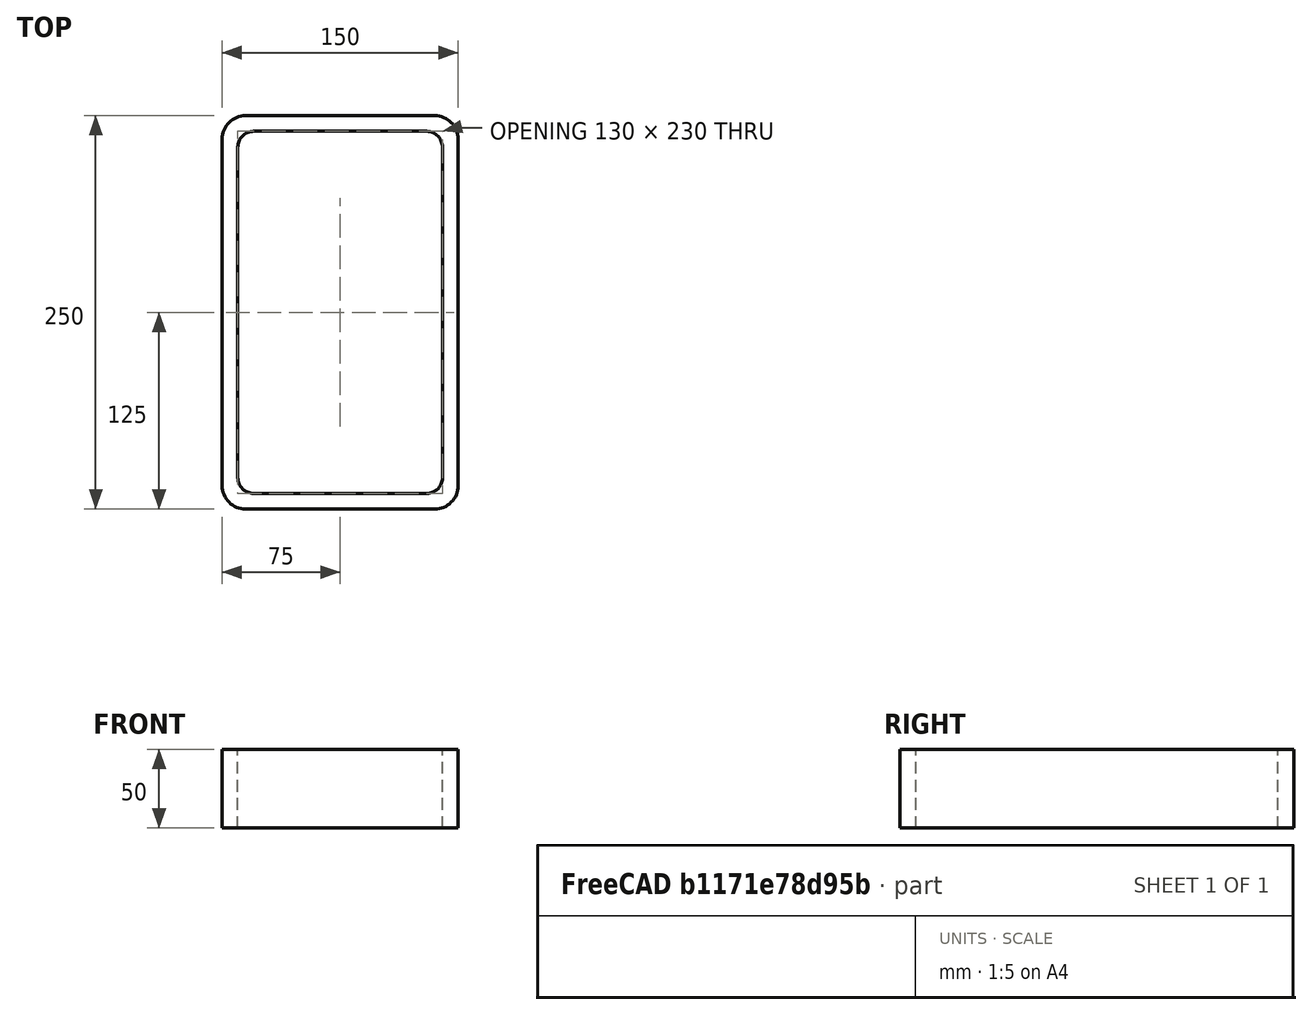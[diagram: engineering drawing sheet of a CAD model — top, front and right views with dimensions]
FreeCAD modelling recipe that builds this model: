
FCSTD DOCUMENT  (FreeCAD 0.15R4671 (Git))
Label: Rectangular hollow section 250x150x10 EN10219 S235JRH
License: All rights reserved
LicenseURL: http://en.wikipedia.org/wiki/All_rights_reserved
objects: Sketcher::SketchObject×1, Part::Extrusion×1
note: 2 computed .brp shape members not serialized (recipe doc carries the construction recipe); baked Part::Feature solids carry a one-line shape summary decoded from their .brp

FEATURE [Sketcher::SketchObject] Sketch
  sketch-geometry (16):
    g0: LineSegment StartX=-55 StartY=115 StartZ=0 EndX=55 EndY=115 EndZ=0
    g1: LineSegment StartX=65 StartY=105 StartZ=0 EndX=65 EndY=-105 EndZ=0
    g2: LineSegment StartX=55 StartY=-115 StartZ=0 EndX=-55 EndY=-115 EndZ=0
    g3: LineSegment StartX=-65 StartY=-105 StartZ=0 EndX=-65 EndY=105 EndZ=0
    g4: LineSegment StartX=-60 StartY=125 StartZ=0 EndX=60 EndY=125 EndZ=0
    g5: LineSegment StartX=75 StartY=110 StartZ=0 EndX=75 EndY=-110 EndZ=0
    g6: LineSegment StartX=60 StartY=-125 StartZ=0 EndX=-60 EndY=-125 EndZ=0
    g7: LineSegment StartX=-75 StartY=-110 StartZ=0 EndX=-75 EndY=110 EndZ=0
    g8: ArcOfCircle CenterX=-55 CenterY=105 CenterZ=0 NormalX=0 NormalY=0 NormalZ=1 Radius=10 StartAngle=1.5708 EndAngle=3.14159
    g9: ArcOfCircle CenterX=55 CenterY=105 CenterZ=0 NormalX=0 NormalY=0 NormalZ=1 Radius=10 StartAngle=0 EndAngle=1.5708
    g10: ArcOfCircle CenterX=55 CenterY=-105 CenterZ=0 NormalX=0 NormalY=0 NormalZ=1 Radius=10 StartAngle=4.71239 EndAngle=6.28319
    g11: ArcOfCircle CenterX=-55 CenterY=-105 CenterZ=0 NormalX=0 NormalY=0 NormalZ=1 Radius=10 StartAngle=3.14159 EndAngle=4.71239
    g12: ArcOfCircle CenterX=60 CenterY=110 CenterZ=0 NormalX=0 NormalY=0 NormalZ=1 Radius=15 StartAngle=0 EndAngle=1.5708
    g13: ArcOfCircle CenterX=60 CenterY=-110 CenterZ=0 NormalX=0 NormalY=0 NormalZ=1 Radius=15 StartAngle=4.71239 EndAngle=6.28319
    g14: ArcOfCircle CenterX=-60 CenterY=-110 CenterZ=0 NormalX=0 NormalY=0 NormalZ=1 Radius=15 StartAngle=3.14159 EndAngle=4.71239
    g15: ArcOfCircle CenterX=-60 CenterY=110 CenterZ=0 NormalX=0 NormalY=0 NormalZ=1 Radius=15 StartAngle=1.5708 EndAngle=3.14159
  constraints (36):
    c: Horizontal(g2)
    c: Vertical(g3)
    c: Horizontal(g6)
    c: Vertical(g7)
    c: Tangent(g3,g8) = 1.5708
    c: Tangent(g0,g8) = 1.5708
    c: Tangent(g0,g9) = 1.5708
    c: Tangent(g1,g9) = 1.5708
    c: Tangent(g1,g10) = 1.5708
    c: Tangent(g2,g10) = 1.5708
    c: Tangent(g2,g11) = 1.5708
    c: Tangent(g3,g11) = 1.5708
    c: Tangent(g4,g12) = 1.5708
    c: Tangent(g5,g12) = 1.5708
    c: Tangent(g5,g13) = 1.5708
    c: Tangent(g6,g13) = 1.5708
    c: Tangent(g6,g14) = 1.5708
    c: Tangent(g7,g14) = 1.5708
    c: Tangent(g7,g15) = 1.5708
    c: Tangent(g4,g15) = 1.5708
    c: Equal(g9,g8)
    c: Equal(g9,g11)
    c: Equal(g9,g10)
    c: Equal(g12,g15)
    c: Equal(g12,g14)
    c: Equal(g12,g13)
    c: Symmetric(g4,g6,g-1)
    c: Symmetric(g7,g5,g-2)
    c: DistanceY(g4,g6) = -250
    c: DistanceX(g7,g5) = 150
    c: Symmetric(g3,g1,g-2)
    c: Symmetric(g0,g2,g-1)
    c: DistanceY(g0,g4) = 10
    c: DistanceX(g5,g1) = -10
    c: Radius(g9) = 10
    c: Radius(g12) = 15
FEATURE [Part::Extrusion] Extrude  label="Rectangular hollow section 250x150x10 EN10219 S235JRH"
  Base = -> Sketch
  Dir = (0,0,50)
  Solid = true
